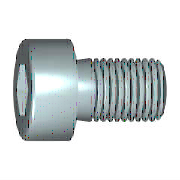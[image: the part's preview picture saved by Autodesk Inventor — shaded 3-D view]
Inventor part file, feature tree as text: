
AUTODESK INVENTOR PART (.ipt)
format: ipt  version: 2022 (Build 260153000, 153)  size: 203,264 bytes
history: native  units: mm (DEFAULTED — no unit token found)
features: sketch x2, other x1, extrude x1, plane x1, fillet x1
ambient origin geometry x7: Origin, YZ Plane, XY Plane, X Axis, Y Axis, Z Axis, Center Point
bodies: Solid1 (feature_tree)
feature tree (6):
  other  "Базовый элемент"
  extrude  "Паз"  Depth=3.9mm
  plane  "Work Plane1"
  fillet  "Fillet2"  Radius=0.429515mm
  sketch  "Эскиз1"
  sketch  "Эскиз2"
